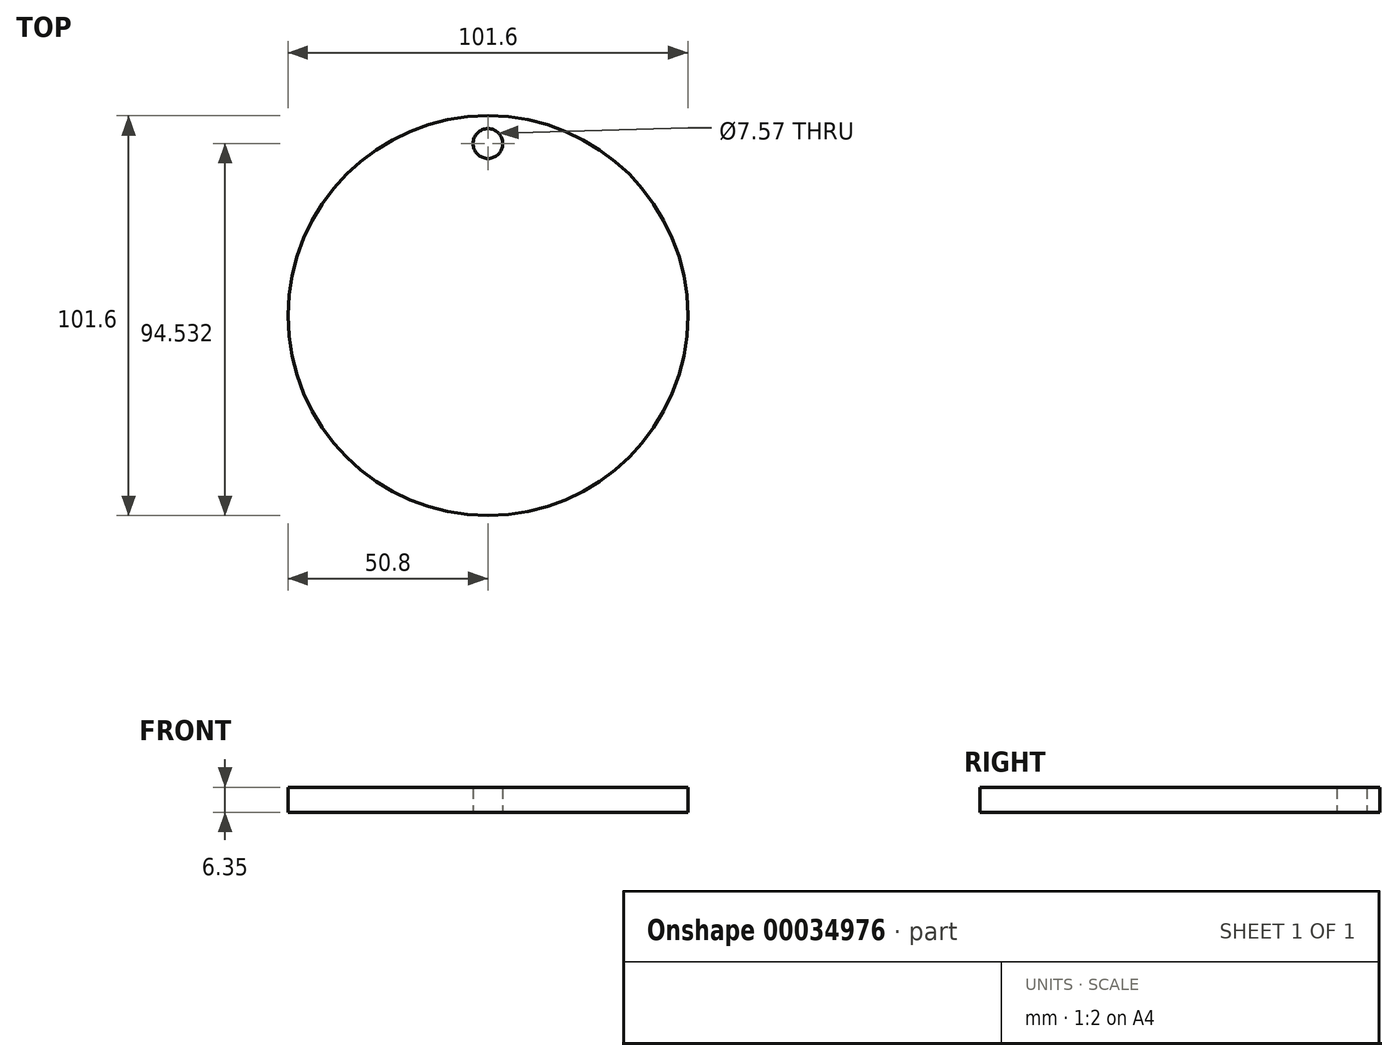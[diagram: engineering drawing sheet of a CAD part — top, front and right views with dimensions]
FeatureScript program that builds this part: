
annotation { "Feature Type Name" : "Feature", "Feature Type Description" : "" }
export const myFeature = defineFeature(function(context is Context, id is Id, definition is map)
    precondition{}
    {
        {
            var Q0;
            Q0=qCreatedBy(makeId("Top.planeOp"),FACE);
            var sketch = newSketch(context, id + "F0", { "sketchPlane" : qUnion([Q0])});
            skCircle(sketch, "E0", {"center": v(0, 0) * mm, "radius": 50.8 * mm});
            skCircle(sketch, "E1", {"center": v(0, 43.73) * mm, "radius": 3.78 * mm});
            skLineSegment(sketch, "E2", {"start": v(-3.78, 43.73) * mm, "end": v(3.78, 43.73) * mm});
            skLineSegment(sketch, "E3", {"start": v(0, 50.8) * mm, "end": v(0, -50.8) * mm});
            skSolve(sketch);
        }
        {
            var Q0;
            Q0=makeQuery(id+"F0.imprint","IMPRINT",FACE,{"disambiguationData":[TD([[makeQuery(id+"F0.imprint","IMPRINT",EDGE,{"derivedFrom":sQuery(id+"F0.wireOp",EDGE,"E0")}),1.0]])]});
            extrude(context, id + "F1", {"entities" : qUnion([Q0]), "depth" : 6.35 * mm});
        }
    });
